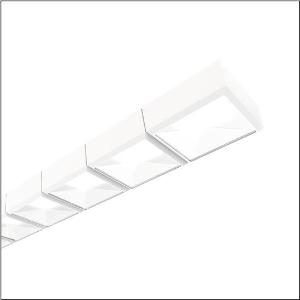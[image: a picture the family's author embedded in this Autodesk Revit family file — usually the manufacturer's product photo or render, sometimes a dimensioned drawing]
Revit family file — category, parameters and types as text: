
# Revit family: scriptus_11_5mz212d04wa
name_source: partatom
category: Lighting Fixtures
units: mm (PartAtom-declared; Revit-internal decimal feet)

## family parameters
Cut with Voids When Loaded = No
Host = Face
Light Source = No
Part Type = Normal
Room Calculation Point = No
Round Connector Dimension = Use Diameter
Shared = No

## types (1)
- Scriptus 11 (1 x LED 4000K / CRI = 80 (unbekannt), 2410 lm, 4000K)
    Apparent Load = 35 VA
    CIE Flux Codes = 82 95 99 100 100
    Color Rendering = 80
    Color Temperature = 4000K
    Default Elevation = 1800 mm
    Description = Scriptus 11, office luminaire, primary optical cover: lenses, CAT 2 (L<= 3000cd/m²), light emission: direct distribution, primary light characteristic: symmetric, installation type: surface-mounted, LED, rated luminous flux: 4.810lm, luminous efficacy: 139lm/W, light colour: 840, colour temperature: 4000K, control gear: DALI, with terminal, 5-pole, mains connection: 230V, AC, 50Hz, rated input power: 35W, housing, luminaire housing, of aluminium, traffic white (RAL 9016), length: 1.658mm, width: 114mm, height: 57mm, protection rating (complete): IP20, insulation class (complete): insulation class I (protective earthing), certification: CE, ENEC, VDE, protection symbol: F, permissible operating ambient temperature: 0..+35°C, standard: EN 50419, packaging unit: 1 piece
    Height = 57 mm
    Lamp = 1 x LED 4000K / CRI >= 80 (unbekannt)
    Lamp Light Flux = 2410 lm
    Lamp count = 1
    Length = 1658 mm
    Luminous efficacy = 139 lm/W
    Manufacturer = Siteco
    ModVariant = No
    Model = 5MZ212D04WA
    Mounting Place = Ceiling
    Mounting Type = Surface mounted
    Number of Poles = 1
    OnlyDefault = Yes
    Power Factor = 1
    Product Name = Scriptus 11
    Product group = office luminaire | ceiling mounted
    ProductGroupID = 301
    Protection Class = Protection class I
    Protection Degree = IP 20
    RLX_Detail_Level = 1
    RLX_Emergency_Light_Flux = 0 lm
    RLX_Emergency_Type = 0
    RLX_Emergency_Type_DB = No
    RlxData = <blob elided: 29449 chars, md5=31bbd2e4>
    Socket = socket
    Standby Power = 0 W
    System Light Flux = 4820 lm
    System Power = 35 W
    Type Comments = Product without accessories
    Type Image = l_1004833.jpg
    URL = http://relux.com
    VarID = ---
    Voltage = 0 V
    Weight = 0.00 kg
    Width = 114 mm

## geometry (parser evidence)
native form markers: Blend x4, Sweep x14
no freeform markers — native parametric forms only
